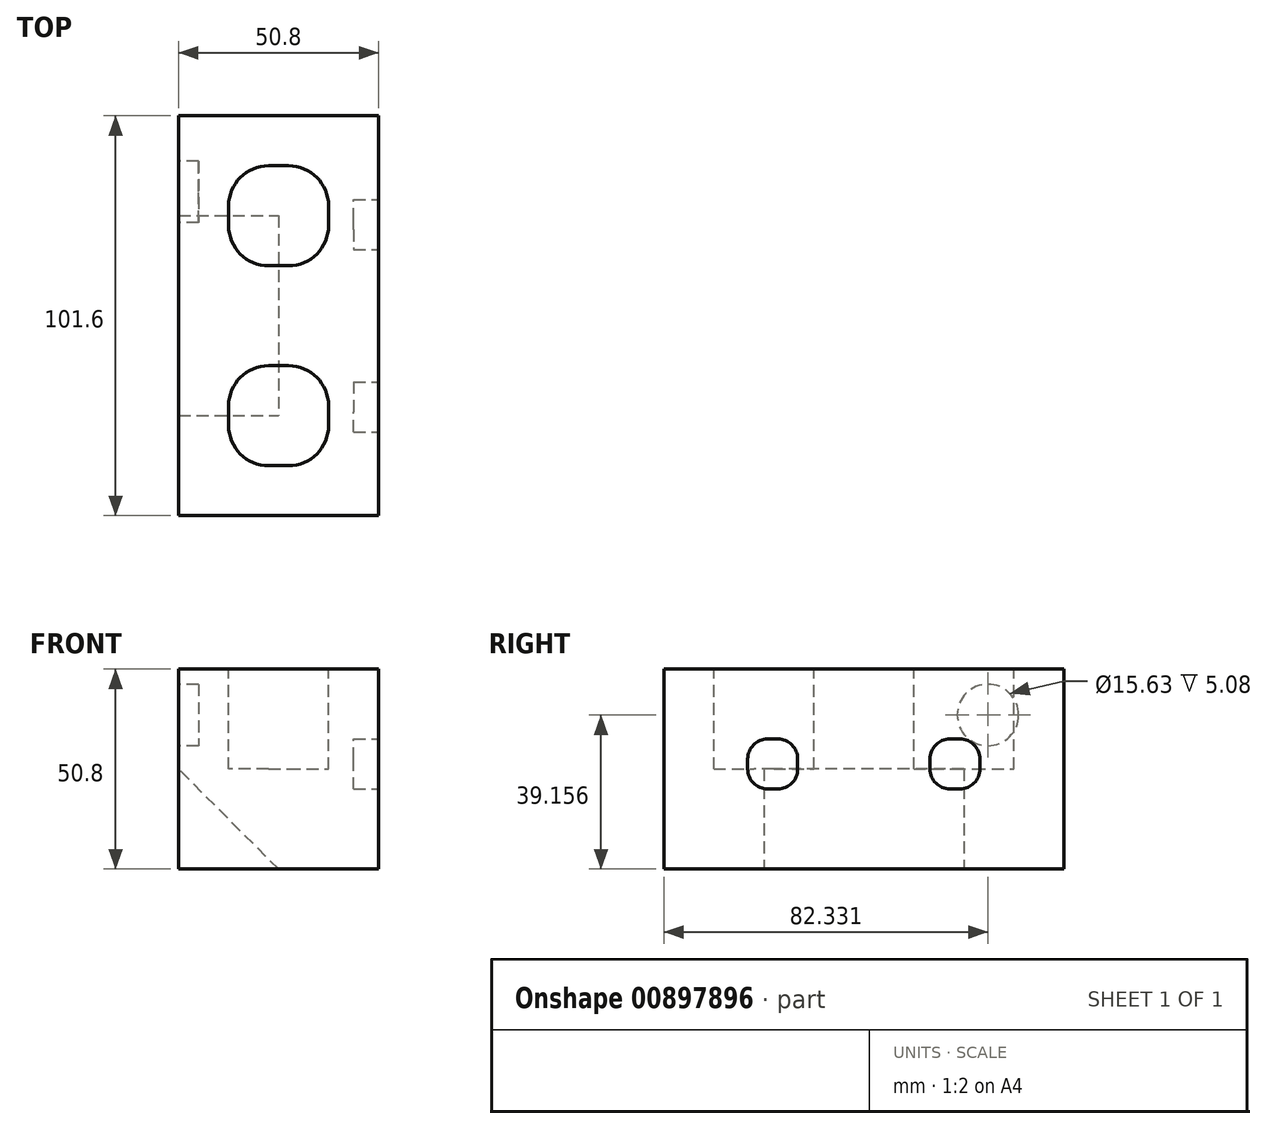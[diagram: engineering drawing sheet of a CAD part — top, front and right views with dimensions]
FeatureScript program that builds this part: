
annotation { "Feature Type Name" : "Feature", "Feature Type Description" : "" }
export const myFeature = defineFeature(function(context is Context, id is Id, definition is map)
    precondition{}
    {
        {
            var Q0;
            Q0=qCreatedBy(makeId("Top.planeOp"),FACE);
            var sketch = newSketch(context, id + "F0", { "sketchPlane" : qUnion([Q0])});
            skLineSegment(sketch, "E0.bottom", {"start": v(0, 0) * mm, "end": v(50.8, 0) * mm});
            skLineSegment(sketch, "E0.top", {"start": v(0, 50.8) * mm, "end": v(50.8, 50.8) * mm});
            skLineSegment(sketch, "E0.left", {"start": v(0, 0) * mm, "end": v(0, 50.8) * mm});
            skLineSegment(sketch, "E0.right", {"start": v(50.8, 0) * mm, "end": v(50.8, 50.8) * mm});
            skSolve(sketch);
        }
        {
            var Q0;
            Q0=makeQuery(id+"F0.imprint","IMPRINT",FACE,{"disambiguationData":[TD([[makeQuery(id+"F0.imprint","IMPRINT",EDGE,{"derivedFrom":sQuery(id+"F0.wireOp",EDGE,"E0.bottom")}),1.0]])]});
            extrude(context, id + "F1", {"entities" : qUnion([Q0]), "depth" : 50.8 * mm});
        }
        {
            var Q0;
            Q0=makeQuery(id+"F1.opExtrude","CAP_FACE",FACE,{"disambiguationData":[OSD([sQuery(id+"F0.wireOp",EDGE,"E0.bottom"),sQuery(id+"F0.wireOp",EDGE,"E0.top"),sQuery(id+"F0.wireOp",EDGE,"E0.left"),sQuery(id+"F0.wireOp",EDGE,"E0.right")])],"isStart":false});
            var sketch = newSketch(context, id + "F2", { "sketchPlane" : qUnion([Q0])});
            skLineSegment(sketch, "E1.bottom", {"start": v(12.7, 12.7) * mm, "end": v(38.1, 12.7) * mm});
            skLineSegment(sketch, "E1.top", {"start": v(12.7, 38.1) * mm, "end": v(38.1, 38.1) * mm});
            skLineSegment(sketch, "E1.left", {"start": v(12.7, 12.7) * mm, "end": v(12.7, 38.1) * mm});
            skLineSegment(sketch, "E1.right", {"start": v(38.1, 12.7) * mm, "end": v(38.1, 38.1) * mm});
            skSolve(sketch);
        }
        {
            var Q0;
            Q0=makeQuery(id+"F2.imprint","IMPRINT",FACE,{"disambiguationData":[TD([[makeQuery(id+"F2.imprint","IMPRINT",EDGE,{"derivedFrom":sQuery(id+"F2.wireOp",EDGE,"E1.bottom")}),1.0]])]});
            extrude(context, id + "F3", {"entities" : qUnion([Q0]), "operationType" : NewBodyOperationType.REMOVE, "oppositeDirection" : true, "depth" : 25.4 * mm});
        }
        {
            var Q0;
            Q0=makeQuery(id+"F3.boolean.opBoolean","COPY",EDGE,{"derivedFrom":makeQuery(id+"F3.opExtrude","SWEPT_EDGE",EDGE,{"disambiguationData":[OSD([sQuery(id+"F2.wireOp",EDGE,"E1.top"),sQuery(id+"F2.wireOp",EDGE,"E1.left")])]})});
            var Q1;
            Q1=makeQuery(id+"F3.boolean.opBoolean","COPY",EDGE,{"derivedFrom":makeQuery(id+"F3.opExtrude","SWEPT_EDGE",EDGE,{"disambiguationData":[OSD([sQuery(id+"F2.wireOp",EDGE,"E1.top"),sQuery(id+"F2.wireOp",EDGE,"E1.right")])]})});
            var Q2;
            Q2=makeQuery(id+"F3.boolean.opBoolean","COPY",EDGE,{"derivedFrom":makeQuery(id+"F3.opExtrude","SWEPT_EDGE",EDGE,{"disambiguationData":[OSD([sQuery(id+"F2.wireOp",EDGE,"E1.bottom"),sQuery(id+"F2.wireOp",EDGE,"E1.left")])]})});
            var Q3;
            Q3=makeQuery(id+"F3.boolean.opBoolean","COPY",EDGE,{"derivedFrom":makeQuery(id+"F3.opExtrude","SWEPT_EDGE",EDGE,{"disambiguationData":[OSD([sQuery(id+"F2.wireOp",EDGE,"E1.bottom"),sQuery(id+"F2.wireOp",EDGE,"E1.right")])]})});
            fillet(context, id + "F4", {"entities" : qUnion([Q0, Q1, Q2, Q3]), "radius" : 10.16 * mm, "tangentPropagation" : true, "allowEdgeOverflow" : false});
        }
        {
            var Q0;
            Q0=makeQuery(id+"F1.opExtrude","SWEPT_FACE",FACE,{"disambiguationData":[OSD([sQuery(id+"F0.wireOp",EDGE,"E0.right")])]});
            var sketch = newSketch(context, id + "F5", { "sketchPlane" : qUnion([Q0])});
            skLineSegment(sketch, "E2.bottom", {"start": v(16.8, 20.35) * mm, "end": v(29.5, 20.35) * mm});
            skLineSegment(sketch, "E2.top", {"start": v(16.8, 33.05) * mm, "end": v(29.5, 33.05) * mm});
            skLineSegment(sketch, "E2.left", {"start": v(16.8, 20.35) * mm, "end": v(16.8, 33.05) * mm});
            skLineSegment(sketch, "E2.right", {"start": v(29.5, 20.35) * mm, "end": v(29.5, 33.05) * mm});
            skSolve(sketch);
        }
        {
            var Q0;
            Q0=qSketchRegion(id+"F5",true);
            extrude(context, id + "F6", {"entities" : qUnion([Q0]), "operationType" : NewBodyOperationType.REMOVE, "oppositeDirection" : true, "depth" : 6.35 * mm});
        }
        {
            var Q0;
            Q0=makeQuery(id+"F6.boolean.opBoolean","COPY",EDGE,{"derivedFrom":makeQuery(id+"F6.opExtrude","SWEPT_EDGE",EDGE,{"disambiguationData":[OSD([sQuery(id+"F5.wireOp",EDGE,"E2.bottom"),sQuery(id+"F5.wireOp",EDGE,"E2.left")])]})});
            var Q1;
            Q1=makeQuery(id+"F6.boolean.opBoolean","COPY",EDGE,{"derivedFrom":makeQuery(id+"F6.opExtrude","SWEPT_EDGE",EDGE,{"disambiguationData":[OSD([sQuery(id+"F5.wireOp",EDGE,"E2.top"),sQuery(id+"F5.wireOp",EDGE,"E2.left")])]})});
            var Q2;
            Q2=makeQuery(id+"F6.boolean.opBoolean","COPY",EDGE,{"derivedFrom":makeQuery(id+"F6.opExtrude","SWEPT_EDGE",EDGE,{"disambiguationData":[OSD([sQuery(id+"F5.wireOp",EDGE,"E2.top"),sQuery(id+"F5.wireOp",EDGE,"E2.right")])]})});
            var Q3;
            Q3=makeQuery(id+"F6.boolean.opBoolean","COPY",EDGE,{"derivedFrom":makeQuery(id+"F6.opExtrude","SWEPT_EDGE",EDGE,{"disambiguationData":[OSD([sQuery(id+"F5.wireOp",EDGE,"E2.bottom"),sQuery(id+"F5.wireOp",EDGE,"E2.right")])]})});
            fillet(context, id + "F7", {"entities" : qUnion([Q0, Q1, Q2, Q3]), "radius" : 5.08 * mm, "tangentPropagation" : true, "allowEdgeOverflow" : false});
        }
        {
            var Q0;
            Q0=makeQuery(id+"F1.opExtrude","SWEPT_FACE",FACE,{"disambiguationData":[OSD([sQuery(id+"F0.wireOp",EDGE,"E0.bottom")])]});
            var sketch = newSketch(context, id + "F8", { "sketchPlane" : qUnion([Q0])});
            skCircle(sketch, "E3", {"center": v(21, 28.58) * mm, "radius": 6.48 * mm});
            skSolve(sketch);
        }
        {
            var Q0;
            Q0=makeQuery(id+"F1.opExtrude","SWEPT_FACE",FACE,{"disambiguationData":[OSD([sQuery(id+"F0.wireOp",EDGE,"E0.bottom")])]});
            var sketch = newSketch(context, id + "F9", { "sketchPlane" : qUnion([Q0])});
            skLineSegment(sketch, "E4", {"start": v(0, 0) * mm, "end": v(25.4, 0) * mm});
            skLineSegment(sketch, "E5", {"start": v(25.4, 0) * mm, "end": v(0, 25.4) * mm});
            skLineSegment(sketch, "E6", {"start": v(0, 25.4) * mm, "end": v(0, 0) * mm});
            skSolve(sketch);
        }
        {
            var Q0;
            Q0=makeQuery(id+"F9.imprint","IMPRINT",FACE,{"disambiguationData":[TD([[makeQuery(id+"F9.imprint","IMPRINT",EDGE,{"derivedFrom":sQuery(id+"F9.wireOp",EDGE,"E4")}),1.0]])]});
            extrude(context, id + "F10", {"entities" : qUnion([Q0]), "operationType" : NewBodyOperationType.REMOVE, "oppositeDirection" : true, "offsetDistance" : 25.4 * mm, "depth" : 25.4 * mm});
        }
        {
            var Q0;
            Q0=makeQuery(id+"F10.boolean.opBoolean","COPY",FACE,{"derivedFrom":makeQuery(id+"F10.opExtrude","SWEPT_FACE",FACE,{"disambiguationData":[OSD([sQuery(id+"F9.wireOp",EDGE,"E5")])]})});
            var sketch = newSketch(context, id + "F11", { "sketchPlane" : qUnion([Q0])});
            skCircle(sketch, "E7", {"center": v(-13.72, 0) * mm, "radius": 6.35 * mm});
            skSolve(sketch);
        }
        {
            var Q0;
            Q0=makeQuery(id+"F1.opExtrude","SWEPT_BODY",BODY,{"disambiguationData":[OSD([sQuery(id+"F0.wireOp",EDGE,"E0.bottom"),sQuery(id+"F0.wireOp",EDGE,"E0.top"),sQuery(id+"F0.wireOp",EDGE,"E0.left"),sQuery(id+"F0.wireOp",EDGE,"E0.right")])]});
            var Q1;
            Q1=makeQuery(id+"F8.imprint","IMPRINT",FACE,{"disambiguationData":[TD([[makeQuery(id+"F8.imprint","IMPRINT",EDGE,{"derivedFrom":sQuery(id+"F8.wireOp",EDGE,"E3")}),-1.0]])]});
            mirror(context, id + "F12", {"operationType" : NewBodyOperationType.ADD, "entities" : qUnion([Q0]), "mirrorPlane" : qUnion([Q1])});
        }
        {
            var Q0;
            {var subQ0=makeQuery(id+"F1.opExtrude","SWEPT_FACE",FACE,{"disambiguationData":[OSD([sQuery(id+"F0.wireOp",EDGE,"E0.left")])]});Q0=makeQuery(id+"F12.boolean.opBoolean","MERGE",FACE,{"derivedFrom":[subQ0,makeQuery(id+"F12.opPattern","COPY",FACE,{"derivedFrom":subQ0,"instanceName":"1"})]});}
            var sketch = newSketch(context, id + "F13", { "sketchPlane" : qUnion([Q0])});
            skCircle(sketch, "E8", {"center": v(-31.53, 39.16) * mm, "radius": 7.82 * mm});
            skSolve(sketch);
        }
        {
            var Q0;
            Q0=makeQuery(id+"F13.imprint","IMPRINT",FACE,{"disambiguationData":[TD([[makeQuery(id+"F13.imprint","IMPRINT",EDGE,{"derivedFrom":sQuery(id+"F13.wireOp",EDGE,"E8")}),1.0]])]});
            extrude(context, id + "F14", {"entities" : qUnion([Q0]), "operationType" : NewBodyOperationType.REMOVE, "oppositeDirection" : true, "depth" : 5.08 * mm, "offsetDistance" : 25.4 * mm});
        }
    });
